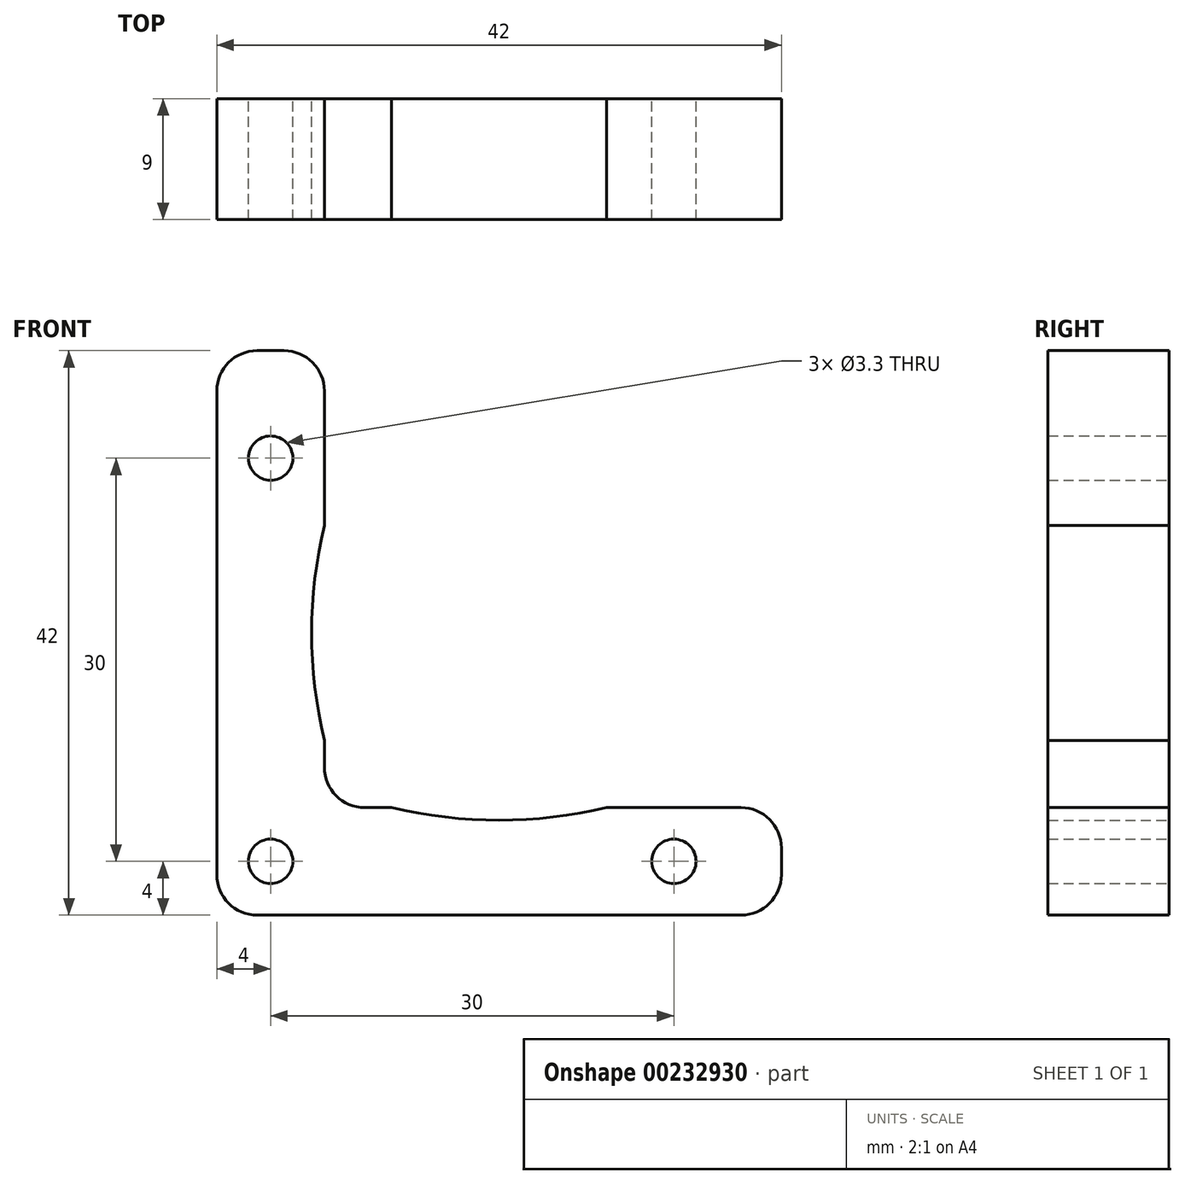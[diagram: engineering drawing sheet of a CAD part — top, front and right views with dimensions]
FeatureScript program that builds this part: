
annotation { "Feature Type Name" : "Feature", "Feature Type Description" : "" }
export const myFeature = defineFeature(function(context is Context, id is Id, definition is map)
    precondition{}
    {
        {
            var Q0;
            Q0=qCreatedBy(makeId("Front.planeOp"),FACE);
            var sketch = newSketch(context, id + "F0", { "sketchPlane" : qUnion([Q0])});
            skLineSegment(sketch, "E0.bottom", {"start": v(0, 0) * mm, "end": v(-34, 0) * mm});
            skLineSegment(sketch, "E0.top", {"start": v(0, -8) * mm, "end": v(-42, -8) * mm});
            skLineSegment(sketch, "E0.left", {"start": v(0, 0) * mm, "end": v(0, -8) * mm});
            skLineSegment(sketch, "E0.right", {"start": v(-42, 0) * mm, "end": v(-42, -8) * mm});
            skLineSegment(sketch, "E1.top", {"start": v(-42, 34) * mm, "end": v(-34, 34) * mm});
            skLineSegment(sketch, "E1.left", {"start": v(-42, 0) * mm, "end": v(-42, 34) * mm});
            skLineSegment(sketch, "E1.right", {"start": v(-34, 0) * mm, "end": v(-34, 34) * mm});
            skPoint(sketch, "E2", {"position": v(-38, 26) * mm});
            skPoint(sketch, "E3", {"position": v(-8, -4) * mm});
            skPoint(sketch, "E4.end.orphan", {"position": v(-38, -4) * mm});
            skPoint(sketch, "E5.orphan", {"position": v(-42, -4) * mm});
            skPoint(sketch, "E6.start.orphan", {"position": v(-38, 34) * mm});
            skPoint(sketch, "E7", {"position": v(-34, 5) * mm});
            skPoint(sketch, "E8", {"position": v(-34, 21) * mm});
            skPoint(sketch, "E9", {"position": v(-29, 0) * mm});
            skPoint(sketch, "E10", {"position": v(-13, 0) * mm});
            skLineSegment(sketch, "E11", {"start": v(-38, 26) * mm, "end": v(-34, 34) * mm});
            skArc(sketch, "E12", {"start": v(-34, 21) * mm, "mid": v(-34.95, 13) * mm, "end": v(-34, 5) * mm});
            skArc(sketch, "E13", {"start": v(-29, 0) * mm, "mid": v(-21, -0.94) * mm, "end": v(-13, 0) * mm});
            skSolve(sketch);
        }
        {
            var Q0;
            Q0=makeQuery(id+"F0.imprint","IMPRINT",FACE,{"disambiguationData":[TD([[makeQuery(id+"F0.imprint","IMPRINT",EDGE,{"derivedFrom":sQuery(id+"F0.wireOp",EDGE,"E0.top")}),-1.0]])]});
            extrude(context, id + "F1", {"entities" : qUnion([Q0]), "depth" : 9 * mm});
        }
        {
            var Q0;
            Q0=makeQuery(id+"F1.opExtrude","SWEPT_EDGE",EDGE,{"disambiguationData":[OSD([sQuery(id+"F0.wireOp",EDGE,"E1.top"),sQuery(id+"F0.wireOp",EDGE,"E1.right")])]});
            var Q1;
            Q1=makeQuery(id+"F1.opExtrude","SWEPT_EDGE",EDGE,{"disambiguationData":[OSD([sQuery(id+"F0.wireOp",EDGE,"E1.top"),sQuery(id+"F0.wireOp",EDGE,"E1.left")])]});
            var Q2;
            Q2=makeQuery(id+"F1.opExtrude","SWEPT_EDGE",EDGE,{"disambiguationData":[OSD([sQuery(id+"F0.wireOp",EDGE,"E0.bottom"),sQuery(id+"F0.wireOp",EDGE,"E0.left")])]});
            var Q3;
            Q3=makeQuery(id+"F1.opExtrude","SWEPT_EDGE",EDGE,{"disambiguationData":[OSD([sQuery(id+"F0.wireOp",EDGE,"E0.top"),sQuery(id+"F0.wireOp",EDGE,"E0.left")])]});
            var Q4;
            Q4=makeQuery(id+"F1.opExtrude","SWEPT_EDGE",EDGE,{"disambiguationData":[OSD([sQuery(id+"F0.wireOp",EDGE,"E0.bottom"),sQuery(id+"F0.wireOp",EDGE,"E1.right")])]});
            var Q5;
            Q5=makeQuery(id+"F1.opExtrude","SWEPT_EDGE",EDGE,{"disambiguationData":[OSD([sQuery(id+"F0.wireOp",EDGE,"E0.top"),sQuery(id+"F0.wireOp",EDGE,"E0.right")])]});
            fillet(context, id + "F2", {"entities" : qUnion([Q0, Q1, Q2, Q3, Q4, Q5]), "radius" : 3 * mm, "tangentPropagation" : true, "allowEdgeOverflow" : false});
        }
        {
            var Q0;
            Q0=sQuery(id+"F0.wireOp",VERTEX,"E2");
            var Q1;
            Q1=sQuery(id+"F0.wireOp",VERTEX,"E4.end.orphan");
            var Q2;
            Q2=sQuery(id+"F0.wireOp",VERTEX,"E3");
            var Q3;
            Q3=makeQuery(id+"F1.opExtrude","SWEPT_BODY",BODY,{"disambiguationData":[OSD([sQuery(id+"F0.wireOp",EDGE,"E0.bottom"),sQuery(id+"F0.wireOp",EDGE,"E0.top"),sQuery(id+"F0.wireOp",EDGE,"E0.left"),sQuery(id+"F0.wireOp",EDGE,"E0.right"),sQuery(id+"F0.wireOp",EDGE,"E1.top"),sQuery(id+"F0.wireOp",EDGE,"E1.left"),sQuery(id+"F0.wireOp",EDGE,"E1.right"),sQuery(id+"F0.wireOp",EDGE,"E12"),sQuery(id+"F0.wireOp",EDGE,"E13")])]});
            hole(context, id + "F3", {"style" : HoleStyle.SIMPLE, "endStyle" : HoleEndStyle.THROUGH, "oppositeDirection" : true, "standardTappedOrClearance" : lookupTablePath({ "standard" : "ISO", "fit" : "Normal", "size" : "M3", "type" : "Clearance" }), "standardBlindInLast" : lookupTablePath({ "fit" : "Standard", "standard" : "ISO", "size" : "M3", "type" : "Clearance" }), "holeDiameter" : 3.3 * mm, "tappedDepth" : 12 * mm, "tapClearance" : 3, "locations" : qUnion([Q0, Q1, Q2]), "scope" : qUnion([Q3])});
        }
    });
